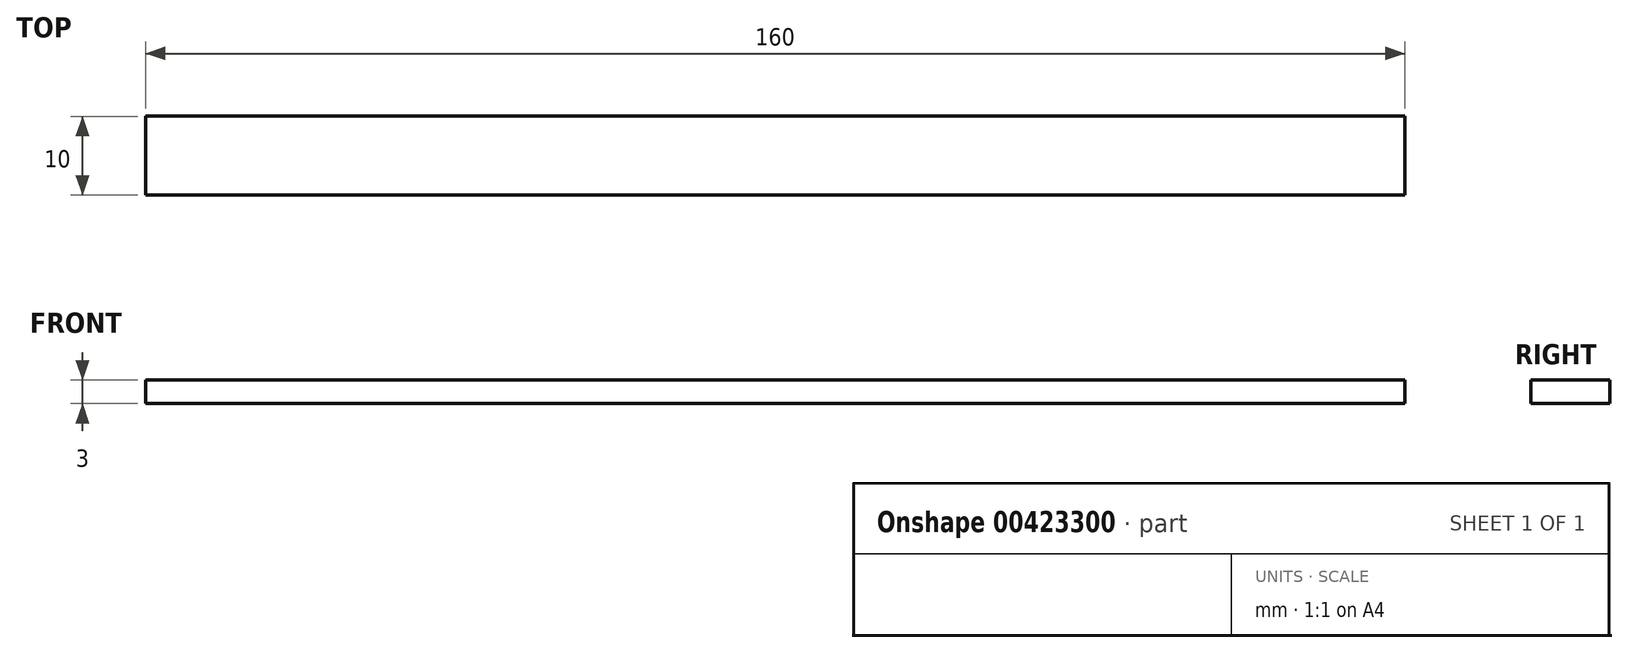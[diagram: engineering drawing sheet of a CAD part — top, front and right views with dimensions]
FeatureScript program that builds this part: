
annotation { "Feature Type Name" : "Feature", "Feature Type Description" : "" }
export const myFeature = defineFeature(function(context is Context, id is Id, definition is map)
    precondition{}
    {
        {
            var Q0;
            Q0=qCreatedBy(makeId("Top.planeOp"),FACE);
            var sketch = newSketch(context, id + "F0", { "sketchPlane" : qUnion([Q0])});
            skLineSegment(sketch, "E0.bottom", {"start": v(-38.53, -46.26) * mm, "end": v(121.47, -46.26) * mm});
            skLineSegment(sketch, "E0.top", {"start": v(-38.53, -56.26) * mm, "end": v(121.47, -56.26) * mm});
            skLineSegment(sketch, "E0.left", {"start": v(-38.53, -46.26) * mm, "end": v(-38.53, -56.26) * mm});
            skLineSegment(sketch, "E0.right", {"start": v(121.47, -46.26) * mm, "end": v(121.47, -56.26) * mm});
            skSolve(sketch);
        }
        {
            var Q0;
            Q0 = qSketchRegion(id + "F0", true);
            extrude(context, id + "F1", {"entities" : qUnion([Q0]), "depth" : 3 * mm});
        }
    });
